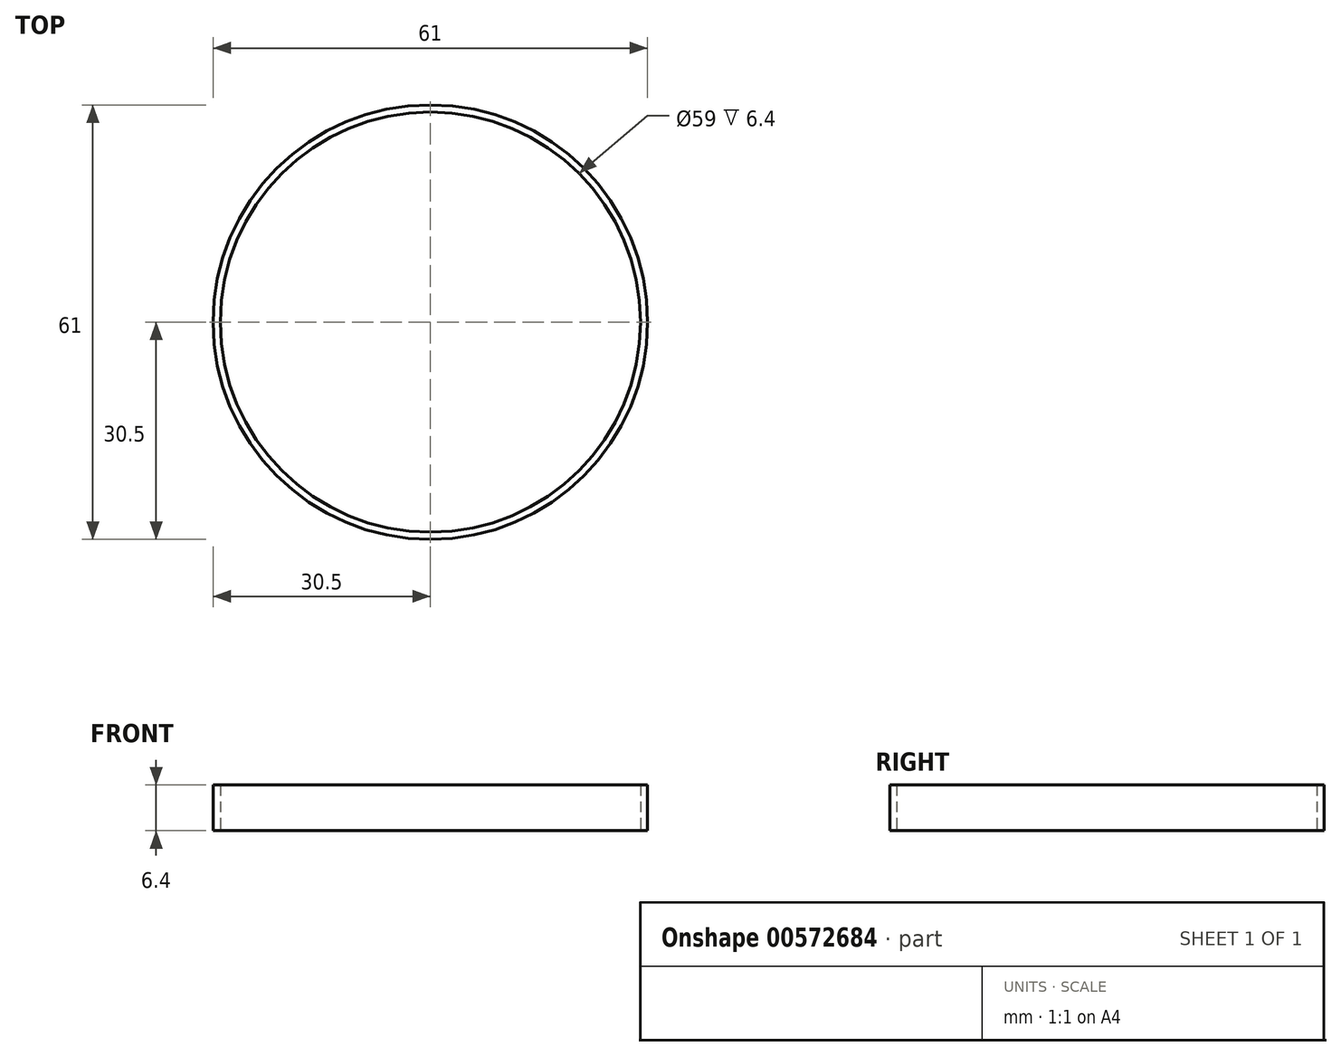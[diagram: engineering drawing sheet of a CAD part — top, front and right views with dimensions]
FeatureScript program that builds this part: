
annotation { "Feature Type Name" : "Feature", "Feature Type Description" : "" }
export const myFeature = defineFeature(function(context is Context, id is Id, definition is map)
    precondition{}
    {
        {
            var Q0;
            Q0=qCreatedBy(makeId("Top.planeOp"),FACE);
            var sketch = newSketch(context, id + "F0", { "sketchPlane" : qUnion([Q0])});
            skCircle(sketch, "E0", {"center": v(0, 0) * mm, "radius": 29.5 * mm});
            skCircle(sketch, "E1", {"center": v(0, 0) * mm, "radius": 30.5 * mm});
            skSolve(sketch);
        }
        {
            var Q0;
            Q0=qSketchRegion(id+"F0",true);
            extrude(context, id + "F1", {"entities" : qUnion([Q0]), "depth" : 6.4 * mm, "offsetDistance" : 25 * mm});
        }
    });
